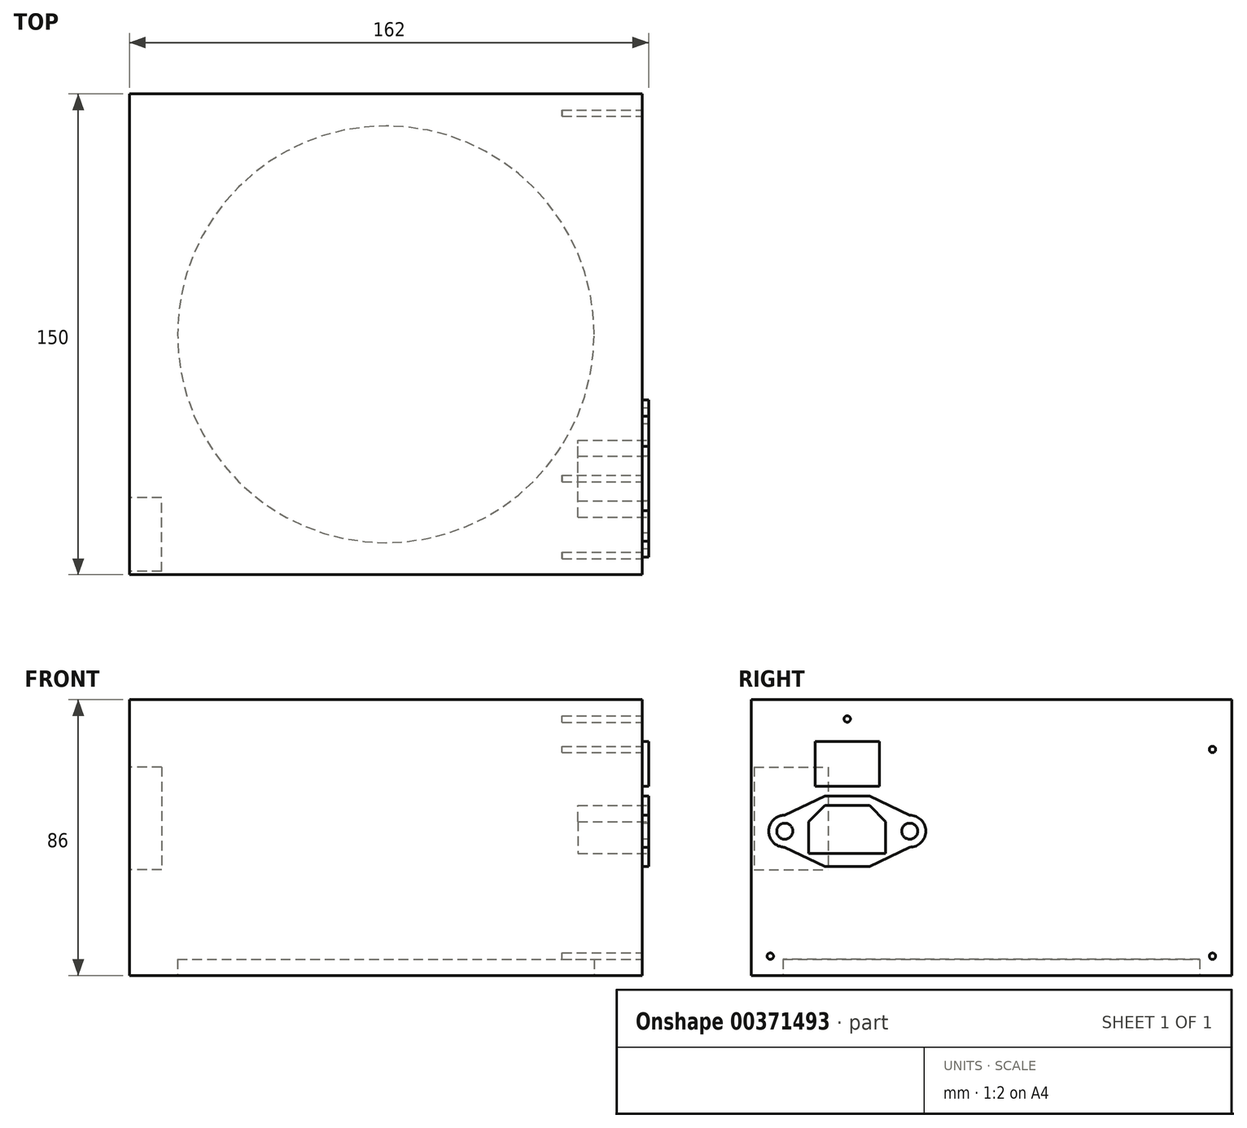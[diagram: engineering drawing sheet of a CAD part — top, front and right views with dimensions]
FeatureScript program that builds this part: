
annotation { "Feature Type Name" : "Feature", "Feature Type Description" : "" }
export const myFeature = defineFeature(function(context is Context, id is Id, definition is map)
    precondition{}
    {
        {
            var Q0;
            Q0=qCreatedBy(makeId("Top.planeOp"),FACE);
            var sketch = newSketch(context, id + "F0", { "sketchPlane" : qUnion([Q0])});
            skLineSegment(sketch, "E0.bottom", {"start": v(13.77, 0) * mm, "end": v(173.77, 0) * mm});
            skLineSegment(sketch, "E0.top", {"start": v(13.77, 150) * mm, "end": v(173.77, 150) * mm});
            skLineSegment(sketch, "E0.left", {"start": v(13.77, 0) * mm, "end": v(13.77, 150) * mm});
            skLineSegment(sketch, "E0.right", {"start": v(173.77, 0) * mm, "end": v(173.77, 150) * mm});
            skSolve(sketch);
        }
        {
            var Q0;
            Q0=makeQuery(id+"F0.imprint","IMPRINT",FACE,{"disambiguationData":[TD([[makeQuery(id+"F0.imprint","IMPRINT",EDGE,{"derivedFrom":sQuery(id+"F0.wireOp",EDGE,"E0.bottom")}),1.0]])]});
            extrude(context, id + "F1", {"entities" : qUnion([Q0]), "depth" : 86 * mm});
        }
        {
            var Q0;
            Q0=makeQuery(id+"F1.opExtrude","SWEPT_FACE",FACE,{"disambiguationData":[OSD([sQuery(id+"F0.wireOp",EDGE,"E0.right")])]});
            var sketch = newSketch(context, id + "F2", { "sketchPlane" : qUnion([Q0])});
            skLineSegment(sketch, "E1.bottom", {"start": v(23, 53) * mm, "end": v(37, 53) * mm});
            skLineSegment(sketch, "E1.top", {"start": v(18, 38) * mm, "end": v(42, 38) * mm});
            skLineSegment(sketch, "E1.left", {"start": v(18, 48) * mm, "end": v(18, 38) * mm});
            skLineSegment(sketch, "E1.right", {"start": v(42, 48) * mm, "end": v(42, 38) * mm});
            skLineSegment(sketch, "E2", {"start": v(18, 48) * mm, "end": v(23, 53) * mm});
            skLineSegment(sketch, "E3", {"start": v(37, 53) * mm, "end": v(42, 48) * mm});
            skPoint(sketch, "E4.orphan", {"position": v(18, 53) * mm});
            skPoint(sketch, "E5.orphan", {"position": v(42, 53) * mm});
            skSolve(sketch);
        }
        {
            var Q0;
            Q0=makeQuery(id+"F2.imprint","IMPRINT",FACE,{"disambiguationData":[TD([[makeQuery(id+"F2.imprint","IMPRINT",EDGE,{"derivedFrom":sQuery(id+"F2.wireOp",EDGE,"E1.bottom")}),-1.0]])]});
            extrude(context, id + "F3", {"entities" : qUnion([Q0]), "operationType" : NewBodyOperationType.REMOVE, "depth" : -20 * mm});
        }
        {
            var Q0;
            Q0=makeQuery(id+"F1.opExtrude","SWEPT_FACE",FACE,{"disambiguationData":[OSD([sQuery(id+"F0.wireOp",EDGE,"E0.right")])]});
            var sketch = newSketch(context, id + "F4", { "sketchPlane" : qUnion([Q0])});
            skLineSegment(sketch, "E6.bottom", {"start": v(20, 59) * mm, "end": v(40, 59) * mm});
            skLineSegment(sketch, "E6.top", {"start": v(20, 73) * mm, "end": v(40, 73) * mm});
            skLineSegment(sketch, "E6.left", {"start": v(20, 59) * mm, "end": v(20, 73) * mm});
            skLineSegment(sketch, "E6.right", {"start": v(40, 59) * mm, "end": v(40, 73) * mm});
            skSolve(sketch);
        }
        {
            var Q0;
            Q0=makeQuery(id+"F4.imprint","IMPRINT",FACE,{"disambiguationData":[TD([[makeQuery(id+"F4.imprint","IMPRINT",EDGE,{"derivedFrom":sQuery(id+"F4.wireOp",EDGE,"E6.bottom")}),1.0]])]});
            extrude(context, id + "F5", {"entities" : qUnion([Q0]), "operationType" : NewBodyOperationType.ADD, "depth" : 2 * mm});
        }
        {
            var Q0;
            Q0=makeQuery(id+"F1.opExtrude","SWEPT_FACE",FACE,{"disambiguationData":[OSD([sQuery(id+"F0.wireOp",EDGE,"E0.right")])]});
            var sketch = newSketch(context, id + "F6", { "sketchPlane" : qUnion([Q0])});
            skArc(sketch, "E7", {"start": v(10.52, 50) * mm, "mid": v(5.5, 45) * mm, "end": v(10.5, 40) * mm});
            skArc(sketch, "E8", {"start": v(49.5, 40) * mm, "mid": v(54.5, 45) * mm, "end": v(49.5, 50) * mm});
            skLineSegment(sketch, "E9.bottom", {"start": v(23, 56) * mm, "end": v(37, 56) * mm});
            skLineSegment(sketch, "E9.top", {"start": v(23, 34) * mm, "end": v(37, 34) * mm});
            skLineSegment(sketch, "E10", {"start": v(10.52, 50) * mm, "end": v(23, 56) * mm});
            skLineSegment(sketch, "E11", {"start": v(10.5, 40) * mm, "end": v(23, 34) * mm});
            skLineSegment(sketch, "E12", {"start": v(49.5, 50) * mm, "end": v(37, 56) * mm});
            skLineSegment(sketch, "E13", {"start": v(49.5, 40) * mm, "end": v(37, 34) * mm});
            skLineSegment(sketch, "E14.bottom", {"start": v(18, 38) * mm, "end": v(42, 38) * mm});
            skLineSegment(sketch, "E14.left", {"start": v(18, 38) * mm, "end": v(18, 48) * mm});
            skLineSegment(sketch, "E14.right", {"start": v(42, 38) * mm, "end": v(42, 48) * mm});
            skLineSegment(sketch, "E15", {"start": v(18, 48) * mm, "end": v(23, 53) * mm});
            skLineSegment(sketch, "E16", {"start": v(23, 53) * mm, "end": v(37, 53) * mm});
            skLineSegment(sketch, "E17", {"start": v(37, 53) * mm, "end": v(42, 48) * mm});
            skCircle(sketch, "E18", {"center": v(10.5, 45) * mm, "radius": 2.5 * mm});
            skCircle(sketch, "E19", {"center": v(49.5, 45) * mm, "radius": 2.5 * mm});
            skSolve(sketch);
        }
        {
            var Q0;
            Q0=makeQuery(id+"F6.imprint","IMPRINT",FACE,{"disambiguationData":[TD([[makeQuery(id+"F6.imprint","IMPRINT",EDGE,{"derivedFrom":sQuery(id+"F6.wireOp",EDGE,"E7")}),1.0]])]});
            extrude(context, id + "F7", {"entities" : qUnion([Q0]), "operationType" : NewBodyOperationType.ADD, "depth" : 2 * mm});
        }
        {
            var Q0;
            {var subQ0=sQuery(id+"F0.wireOp",EDGE,"E0.bottom");var subQ1=sQuery(id+"F0.wireOp",EDGE,"E0.right");Q0=makeQuery(id+"F7.boolean.opBoolean","SPLIT",FACE,{"disambiguationData":[TD([makeQuery(id+"F1.opExtrude","SWEPT_FACE",FACE,{"disambiguationData":[OSD([subQ0])]})])],"derivedFrom":makeQuery(id+"F1.opExtrude","SWEPT_FACE",FACE,{"disambiguationData":[OSD([subQ1])]})});}
            var sketch = newSketch(context, id + "F8", { "sketchPlane" : qUnion([Q0])});
            skCircle(sketch, "E20", {"center": v(30, 80) * mm, "radius": 1 * mm});
            skCircle(sketch, "E21", {"center": v(6, 6) * mm, "radius": 1 * mm});
            skCircle(sketch, "E22", {"center": v(144, 70.5) * mm, "radius": 1 * mm});
            skCircle(sketch, "E23", {"center": v(144, 6) * mm, "radius": 1 * mm});
            skSolve(sketch);
        }
        {
            var Q0;
            Q0 = qSketchRegion(id + "F8", true);
            extrude(context, id + "F9", {"entities" : qUnion([Q0]), "operationType" : NewBodyOperationType.REMOVE, "oppositeDirection" : true, "depth" : 25 * mm});
        }
        {
            var Q0;
            Q0=makeQuery(id+"F1.opExtrude","SWEPT_FACE",FACE,{"disambiguationData":[OSD([sQuery(id+"F0.wireOp",EDGE,"E0.left")])]});
            var sketch = newSketch(context, id + "F10", { "sketchPlane" : qUnion([Q0])});
            skLineSegment(sketch, "E24.bottom", {"start": v(-1, 65) * mm, "end": v(-24, 65) * mm});
            skLineSegment(sketch, "E24.top", {"start": v(-1, 33) * mm, "end": v(-24, 33) * mm});
            skLineSegment(sketch, "E24.left", {"start": v(-1, 65) * mm, "end": v(-1, 33) * mm});
            skLineSegment(sketch, "E24.right", {"start": v(-24, 65) * mm, "end": v(-24, 33) * mm});
            skSolve(sketch);
        }
        {
            var Q0;
            Q0=makeQuery(id+"F10.imprint","IMPRINT",FACE,{"disambiguationData":[TD([[makeQuery(id+"F10.imprint","IMPRINT",EDGE,{"derivedFrom":sQuery(id+"F10.wireOp",EDGE,"E24.bottom")}),1.0]])]});
            extrude(context, id + "F11", {"entities" : qUnion([Q0]), "operationType" : NewBodyOperationType.REMOVE, "oppositeDirection" : true, "depth" : 10 * mm});
        }
        {
            var Q0;
            Q0=makeQuery(id+"F1.opExtrude","CAP_FACE",FACE,{"disambiguationData":[OSD([sQuery(id+"F0.wireOp",EDGE,"E0.bottom"),sQuery(id+"F0.wireOp",EDGE,"E0.top"),sQuery(id+"F0.wireOp",EDGE,"E0.left"),sQuery(id+"F0.wireOp",EDGE,"E0.right")])],"isStart":true});
            var sketch = newSketch(context, id + "F12", { "sketchPlane" : qUnion([Q0])});
            skCircle(sketch, "E25", {"center": v(93.77, -75) * mm, "radius": 65 * mm});
            skPoint(sketch, "E25.centerSnap0", {"position": v(173.77, -75) * mm});
            skPoint(sketch, "E25.centerSnap1", {"position": v(93.77, 0) * mm});
            skSolve(sketch);
        }
        {
            var Q0;
            Q0=makeQuery(id+"F12.imprint","IMPRINT",FACE,{"disambiguationData":[TD([[makeQuery(id+"F12.imprint","IMPRINT",EDGE,{"derivedFrom":sQuery(id+"F12.wireOp",EDGE,"E25")}),1.0]])]});
            extrude(context, id + "F13", {"entities" : qUnion([Q0]), "operationType" : NewBodyOperationType.REMOVE, "oppositeDirection" : true, "depth" : 5 * mm});
        }
    });
